FCSTD DOCUMENT  (FreeCAD 0.18R16131 (Git))
Label: temp part
License: All rights reserved
LicenseURL: http://en.wikipedia.org/wiki/All_rights_reserved
objects: Part::Part2DObjectPython×54, Part::Mirroring×27, App::DocumentObjectGroup×2
note: 81 computed .brp shape members not serialized (recipe doc carries the construction recipe); baked Part::Feature solids carry a one-line shape summary decoded from their .brp

FEATURE [Part::Part2DObjectPython] Circle  label="Hole-mount-1"  # Draft 2D object (typed FeaturePython)
  FirstAngle = 0
  LastAngle = 0
  MakeFace = false
  Placement = pos=(10,150.125,0) rot=(0,0,1;0rad)
  Radius = 1.6
FEATURE [Part::Part2DObjectPython] Rectangle  label="Edge"  # Draft 2D object (typed FeaturePython)
  ChamferSize = 0
  Columns = 1
  FilletRadius = 0
  Height = 160.12
  Length = 90
  MakeFace = false
  Rows = 1
FEATURE [Part::Part2DObjectPython] Circle001  label="Hole-mount-2"  # Draft 2D object (typed FeaturePython)
  FirstAngle = 0
  LastAngle = 0
  MakeFace = false
  Placement = pos=(80,150.125,0) rot=(0,0,1;0rad)
  Radius = 1.6
FEATURE [Part::Part2DObjectPython] Circle002  label="Hole-mount-3"  # Draft 2D object (typed FeaturePython)
  FirstAngle = 0
  LastAngle = 0
  MakeFace = false
  Placement = pos=(80,10,0) rot=(0,0,1;0rad)
  Radius = 1.6
FEATURE [Part::Part2DObjectPython] Circle003  label="Hole-mount-4"  # Draft 2D object (typed FeaturePython)
  FirstAngle = 0
  LastAngle = 0
  MakeFace = false
  Placement = pos=(10,10,0) rot=(0,0,1;0rad)
  Radius = 1.6
FEATURE [Part::Part2DObjectPython] Circle004  label="Hole-mount-VREG-board-1"  # Draft 2D object (typed FeaturePython)
  FirstAngle = 0
  LastAngle = 0
  MakeFace = false
  Placement = pos=(80,141.825,0) rot=(0,0,1;0rad)
  Radius = 1.6
FEATURE [Part::Part2DObjectPython] Circle005  label="Hole-mount-VREG-board-2"  # Draft 2D object (typed FeaturePython)
  FirstAngle = 0
  LastAngle = 0
  MakeFace = false
  Placement = pos=(10,81.825,0) rot=(0,0,1;0rad)
  Radius = 1.6
FEATURE [Part::Part2DObjectPython] Circle006  label="OLED-origin-Ja"  # Draft 2D object (typed FeaturePython)
  FirstAngle = 0
  LastAngle = 0
  MakeFace = false
  Placement = pos=(41.19,143.13,0) rot=(0,0,1;0rad)
  Radius = 0.5
FEATURE [Part::Part2DObjectPython] Circle007  label="VREG-origin-Ja"  # Draft 2D object (typed FeaturePython)
  FirstAngle = 0
  LastAngle = 0
  MakeFace = false
  Placement = pos=(68.5,80.64,0) rot=(0,0,1;0rad)
  Radius = 0.5
FEATURE [Part::Part2DObjectPython] Circle008  label="Hole-gizduinox-1"  # Draft 2D object (typed FeaturePython)
  FirstAngle = 0
  LastAngle = 0
  MakeFace = false
  Placement = pos=(18.9,57.08,0) rot=(0,0,1;0rad)
  Radius = 1.6
FEATURE [Part::Part2DObjectPython] Circle009  label="Hole-gizduinox-2"  # Draft 2D object (typed FeaturePython)
  FirstAngle = 0
  LastAngle = 0
  MakeFace = false
  Placement = pos=(78.2,70.58,0) rot=(0,0,1;0rad)
  Radius = 1.6
FEATURE [Part::Part2DObjectPython] Circle010  label="Hole-gizduinox-3"  # Draft 2D object (typed FeaturePython)
  FirstAngle = 0
  LastAngle = 0
  MakeFace = false
  Placement = pos=(78.25,24.58,0) rot=(0,0,1;0rad)
  Radius = 1.6
FEATURE [Part::Part2DObjectPython] Circle011  label="Hole-gizduinox-4"  # Draft 2D object (typed FeaturePython)
  FirstAngle = 0
  LastAngle = 0
  MakeFace = false
  Placement = pos=(18.9,29.18,0) rot=(0,0,1;0rad)
  Radius = 1.6
FEATURE [Part::Part2DObjectPython] Circle012  label="gizduino-origin-J1a"  # Draft 2D object (typed FeaturePython)
  FirstAngle = 0
  LastAngle = 0
  MakeFace = false
  Placement = pos=(21.5,72.38,0) rot=(0,0,1;0rad)
  Radius = 0.5
FEATURE [Part::Part2DObjectPython] Circle013  label="gizduino-origin-J2a"  # Draft 2D object (typed FeaturePython)
  FirstAngle = 0
  LastAngle = 0
  MakeFace = false
  Placement = pos=(43.34,72.38,0) rot=(0,0,1;0rad)
  Radius = 0.5
FEATURE [Part::Part2DObjectPython] Circle014  label="gizduino-origin-J3a"  # Draft 2D object (typed FeaturePython)
  FirstAngle = 0
  LastAngle = 0
  MakeFace = false
  Placement = pos=(39.28,24.12,0) rot=(0,0,1;0rad)
  Radius = 0.5
FEATURE [Part::Part2DObjectPython] Circle015  label="gizduino-origin-J4a"  # Draft 2D object (typed FeaturePython)
  FirstAngle = 0
  LastAngle = 0
  MakeFace = false
  Placement = pos=(16.42,24.12,0) rot=(0,0,1;0rad)
  Radius = 0.5
FEATURE [Part::Part2DObjectPython] Circle016  label="gizduino-origin-J5a"  # Draft 2D object (typed FeaturePython)
  FirstAngle = 0
  LastAngle = 0
  MakeFace = false
  Placement = pos=(11.34,67.3,0) rot=(0,0,1;0rad)
  Radius = 0.5
FEATURE [Part::Part2DObjectPython] Circle017  label="RFID-origin-J1a"  # Draft 2D object (typed FeaturePython)
  FirstAngle = 0
  LastAngle = 0
  MakeFace = false
  Placement = pos=(36.11,16.37,0) rot=(0,0,1;0rad)
  Radius = 0.5
FEATURE [Part::Part2DObjectPython] Circle018  label="RFID-origin-J1b"  # Draft 2D object (typed FeaturePython)
  FirstAngle = 0
  LastAngle = 0
  MakeFace = false
  Placement = pos=(53.89,16.37,0) rot=(0,0,1;0rad)
  Radius = 0.5
FEATURE [Part::Part2DObjectPython] Circle019  label="OLED-origin-Jb"  # Draft 2D object (typed FeaturePython)
  FirstAngle = 0
  LastAngle = 0
  MakeFace = false
  Placement = pos=(48.81,143.13,0) rot=(0,0,1;0rad)
  Radius = 0.5
FEATURE [Part::Part2DObjectPython] Circle020  label="VREG-origin-Jb"  # Draft 2D object (typed FeaturePython)
  FirstAngle = 0
  LastAngle = 0
  MakeFace = false
  Placement = pos=(73.58,80.64,0) rot=(0,0,1;0rad)
  Radius = 0.5
FEATURE [Part::Part2DObjectPython] Circle021  label="gizduino-origin-J1b"  # Draft 2D object (typed FeaturePython)
  FirstAngle = 0
  LastAngle = 0
  MakeFace = false
  Placement = pos=(39.28,72.38,0) rot=(0,0,1;0rad)
  Radius = 0.5
FEATURE [Part::Part2DObjectPython] Circle022  label="gizduino-origin-J2b"  # Draft 2D object (typed FeaturePython)
  FirstAngle = 0
  LastAngle = 0
  MakeFace = false
  Placement = pos=(61.12,72.38,0) rot=(0,0,1;0rad)
  Radius = 0.5
FEATURE [Part::Part2DObjectPython] Circle023  label="gizduino-origin-J3b"  # Draft 2D object (typed FeaturePython)
  FirstAngle = 0
  LastAngle = 0
  MakeFace = false
  Placement = pos=(51.98,24.12,0) rot=(0,0,1;0rad)
  Radius = 0.5
FEATURE [Part::Part2DObjectPython] Circle024  label="gizduino-origin-J4b"  # Draft 2D object (typed FeaturePython)
  FirstAngle = 0
  LastAngle = 0
  MakeFace = false
  Placement = pos=(34.2,24.12,0) rot=(0,0,1;0rad)
  Radius = 0.5
FEATURE [Part::Part2DObjectPython] Circle025  label="gizduino-origin-J5b"  # Draft 2D object (typed FeaturePython)
  FirstAngle = 0
  LastAngle = 0
  MakeFace = false
  Placement = pos=(8.8,67.3,0) rot=(0,0,1;0rad)
  Radius = 0.5
FEATURE [App::DocumentObjectGroup] Group
  Group = -> [Circle,Rectangle,Circle001,Circle002,Circle003,Circle004,Circle005,Circle006,Circle007,Circle008,Circle009,Circle010,Circle011,Circle012,Circle013,Circle014,Circle015,Circle016,Circle017,Circle018,Circle019,Circle020,Circle021,Circle022,Circle023,Circle024,Circle025]
FEATURE [Part::Part2DObjectPython] Circle026  label="Hole-mount-005"  # Draft 2D object (typed FeaturePython)
  FirstAngle = 0
  LastAngle = 0
  MakeFace = false
  Placement = pos=(80,10,0) rot=(0,0,1;0rad)
  Radius = 1.6
FEATURE [Part::Part2DObjectPython] Circle027  label="gizduino-origin-J2a001"  # Draft 2D object (typed FeaturePython)
  FirstAngle = 0
  LastAngle = 0
  MakeFace = false
  Placement = pos=(43.34,72.38,0) rot=(0,0,1;0rad)
  Radius = 0.5
FEATURE [Part::Part2DObjectPython] Circle028  label="Hole-mount-006"  # Draft 2D object (typed FeaturePython)
  FirstAngle = 0
  LastAngle = 0
  MakeFace = false
  Placement = pos=(80,150.125,0) rot=(0,0,1;0rad)
  Radius = 1.6
FEATURE [Part::Part2DObjectPython] Circle029  label="Hole-mount-007"  # Draft 2D object (typed FeaturePython)
  FirstAngle = 0
  LastAngle = 0
  MakeFace = false
  Placement = pos=(10,150.125,0) rot=(0,0,1;0rad)
  Radius = 1.6
FEATURE [Part::Part2DObjectPython] Circle030  label="Hole-mount-008"  # Draft 2D object (typed FeaturePython)
  FirstAngle = 0
  LastAngle = 0
  MakeFace = false
  Placement = pos=(10,10,0) rot=(0,0,1;0rad)
  Radius = 1.6
FEATURE [Part::Part2DObjectPython] Circle031  label="Hole-mount-VREG-board-003"  # Draft 2D object (typed FeaturePython)
  FirstAngle = 0
  LastAngle = 0
  MakeFace = false
  Placement = pos=(10,81.825,0) rot=(0,0,1;0rad)
  Radius = 1.6
FEATURE [Part::Part2DObjectPython] Circle032  label="VREG-origin-Ja001"  # Draft 2D object (typed FeaturePython)
  FirstAngle = 0
  LastAngle = 0
  MakeFace = false
  Placement = pos=(68.5,80.64,0) rot=(0,0,1;0rad)
  Radius = 0.5
FEATURE [Part::Part2DObjectPython] Circle033  label="gizduino-origin-J1a001"  # Draft 2D object (typed FeaturePython)
  FirstAngle = 0
  LastAngle = 0
  MakeFace = false
  Placement = pos=(21.5,72.38,0) rot=(0,0,1;0rad)
  Radius = 0.5
FEATURE [Part::Part2DObjectPython] Circle034  label="Hole-gizduinox-005"  # Draft 2D object (typed FeaturePython)
  FirstAngle = 0
  LastAngle = 0
  MakeFace = false
  Placement = pos=(78.2,70.58,0) rot=(0,0,1;0rad)
  Radius = 1.6
FEATURE [Part::Part2DObjectPython] Circle035  label="RFID-origin-J1a001"  # Draft 2D object (typed FeaturePython)
  FirstAngle = 0
  LastAngle = 0
  MakeFace = false
  Placement = pos=(36.11,16.37,0) rot=(0,0,1;0rad)
  Radius = 0.5
FEATURE [Part::Part2DObjectPython] Circle036  label="RFID-origin-J1b001"  # Draft 2D object (typed FeaturePython)
  FirstAngle = 0
  LastAngle = 0
  MakeFace = false
  Placement = pos=(53.89,16.37,0) rot=(0,0,1;0rad)
  Radius = 0.5
FEATURE [Part::Part2DObjectPython] Circle037  label="Hole-mount-VREG-board-004"  # Draft 2D object (typed FeaturePython)
  FirstAngle = 0
  LastAngle = 0
  MakeFace = false
  Placement = pos=(80,141.825,0) rot=(0,0,1;0rad)
  Radius = 1.6
FEATURE [Part::Part2DObjectPython] Circle038  label="Hole-gizduinox-006"  # Draft 2D object (typed FeaturePython)
  FirstAngle = 0
  LastAngle = 0
  MakeFace = false
  Placement = pos=(18.9,57.08,0) rot=(0,0,1;0rad)
  Radius = 1.6
FEATURE [Part::Part2DObjectPython] Circle039  label="Hole-gizduinox-007"  # Draft 2D object (typed FeaturePython)
  FirstAngle = 0
  LastAngle = 0
  MakeFace = false
  Placement = pos=(78.25,24.58,0) rot=(0,0,1;0rad)
  Radius = 1.6
FEATURE [Part::Part2DObjectPython] Circle040  label="OLED-origin-Ja001"  # Draft 2D object (typed FeaturePython)
  FirstAngle = 0
  LastAngle = 0
  MakeFace = false
  Placement = pos=(41.19,143.13,0) rot=(0,0,1;0rad)
  Radius = 0.5
FEATURE [Part::Part2DObjectPython] Circle041  label="Hole-gizduinox-008"  # Draft 2D object (typed FeaturePython)
  FirstAngle = 0
  LastAngle = 0
  MakeFace = false
  Placement = pos=(18.9,29.18,0) rot=(0,0,1;0rad)
  Radius = 1.6
FEATURE [Part::Part2DObjectPython] Rectangle001  label="Edge001"  # Draft 2D object (typed FeaturePython)
  ChamferSize = 0
  Columns = 1
  FilletRadius = 0
  Height = 160.12
  Length = 90
  MakeFace = false
  Rows = 1
FEATURE [Part::Part2DObjectPython] Circle042  label="gizduino-origin-J3a001"  # Draft 2D object (typed FeaturePython)
  FirstAngle = 0
  LastAngle = 0
  MakeFace = false
  Placement = pos=(39.28,24.12,0) rot=(0,0,1;0rad)
  Radius = 0.5
FEATURE [Part::Part2DObjectPython] Circle043  label="gizduino-origin-J5a001"  # Draft 2D object (typed FeaturePython)
  FirstAngle = 0
  LastAngle = 0
  MakeFace = false
  Placement = pos=(11.34,67.3,0) rot=(0,0,1;0rad)
  Radius = 0.5
FEATURE [Part::Part2DObjectPython] Circle044  label="OLED-origin-Jb001"  # Draft 2D object (typed FeaturePython)
  FirstAngle = 0
  LastAngle = 0
  MakeFace = false
  Placement = pos=(48.81,143.13,0) rot=(0,0,1;0rad)
  Radius = 0.5
FEATURE [Part::Part2DObjectPython] Circle045  label="gizduino-origin-J4a001"  # Draft 2D object (typed FeaturePython)
  FirstAngle = 0
  LastAngle = 0
  MakeFace = false
  Placement = pos=(16.42,24.12,0) rot=(0,0,1;0rad)
  Radius = 0.5
FEATURE [Part::Part2DObjectPython] Circle046  label="gizduino-origin-J1b001"  # Draft 2D object (typed FeaturePython)
  FirstAngle = 0
  LastAngle = 0
  MakeFace = false
  Placement = pos=(39.28,72.38,0) rot=(0,0,1;0rad)
  Radius = 0.5
FEATURE [Part::Part2DObjectPython] Circle047  label="VREG-origin-Jb001"  # Draft 2D object (typed FeaturePython)
  FirstAngle = 0
  LastAngle = 0
  MakeFace = false
  Placement = pos=(73.58,80.64,0) rot=(0,0,1;0rad)
  Radius = 0.5
FEATURE [Part::Part2DObjectPython] Circle048  label="gizduino-origin-J2b001"  # Draft 2D object (typed FeaturePython)
  FirstAngle = 0
  LastAngle = 0
  MakeFace = false
  Placement = pos=(61.12,72.38,0) rot=(0,0,1;0rad)
  Radius = 0.5
FEATURE [Part::Part2DObjectPython] Circle049  label="gizduino-origin-J3b001"  # Draft 2D object (typed FeaturePython)
  FirstAngle = 0
  LastAngle = 0
  MakeFace = false
  Placement = pos=(51.98,24.12,0) rot=(0,0,1;0rad)
  Radius = 0.5
FEATURE [Part::Part2DObjectPython] Circle050  label="gizduino-origin-J5b001"  # Draft 2D object (typed FeaturePython)
  FirstAngle = 0
  LastAngle = 0
  MakeFace = false
  Placement = pos=(8.8,67.3,0) rot=(0,0,1;0rad)
  Radius = 0.5
FEATURE [Part::Part2DObjectPython] Circle051  label="gizduino-origin-J4b001"  # Draft 2D object (typed FeaturePython)
  FirstAngle = 0
  LastAngle = 0
  MakeFace = false
  Placement = pos=(34.2,24.12,0) rot=(0,0,1;0rad)
  Radius = 0.5
FEATURE [App::DocumentObjectGroup] Group001  label="Mirror"
  Group = -> [Circle029,Rectangle001,Circle028,Circle026,Circle030,Circle037,Circle031,Circle040,Circle032,Circle038,Circle034,Circle039,Circle041,Circle033,Circle027,Circle042,Circle045,Circle043,Circle035,Circle036,Circle044,Circle047,Circle046,Circle048,Circle049,Circle051,Circle050]
FEATURE [Part::Mirroring] mirror  label="Mirror of Hole-mount-007"
  Base = (90,160.12,0)
  Normal = (-1,1e-16,0)
  Source = -> Circle029
FEATURE [Part::Mirroring] mirror001  label="Mirror of Hole-mount-005"
  Base = (90,160.12,0)
  Normal = (-1,1e-16,0)
  Source = -> Circle026
FEATURE [Part::Mirroring] mirror002  label="Mirror of gizduino-origin-J4a001"
  Base = (90,160.12,0)
  Normal = (-1,1e-16,0)
  Source = -> Circle045
FEATURE [Part::Mirroring] mirror003  label="Mirror of Edge001"
  Base = (90,160.12,0)
  Normal = (-1,1e-16,0)
  Source = -> Rectangle001
FEATURE [Part::Mirroring] mirror004  label="Mirror of VREG-origin-Jb001"
  Base = (90,160.12,0)
  Normal = (-1,1e-16,0)
  Source = -> Circle047
FEATURE [Part::Mirroring] mirror005  label="Mirror of OLED-origin-Ja001"
  Base = (90,160.12,0)
  Normal = (-1,1e-16,0)
  Source = -> Circle040
FEATURE [Part::Mirroring] mirror006  label="Mirror of Hole-gizduinox-006"
  Base = (90,160.12,0)
  Normal = (-1,1e-16,0)
  Source = -> Circle038
FEATURE [Part::Mirroring] mirror007  label="Mirror of Hole-gizduinox-007"
  Base = (90,160.12,0)
  Normal = (-1,1e-16,0)
  Source = -> Circle039
FEATURE [Part::Mirroring] mirror008  label="Mirror of gizduino-origin-J5a001"
  Base = (90,160.12,0)
  Normal = (-1,1e-16,0)
  Source = -> Circle043
FEATURE [Part::Mirroring] mirror009  label="Mirror of Hole-gizduinox-008"
  Base = (90,160.12,0)
  Normal = (-1,1e-16,0)
  Source = -> Circle041
FEATURE [Part::Mirroring] mirror010  label="Mirror of gizduino-origin-J1b001"
  Base = (90,160.12,0)
  Normal = (-1,1e-16,0)
  Source = -> Circle046
FEATURE [Part::Mirroring] mirror011  label="Mirror of Hole-mount-006"
  Base = (90,160.12,0)
  Normal = (-1,1e-16,0)
  Source = -> Circle028
FEATURE [Part::Mirroring] mirror012  label="Mirror of gizduino-origin-J5b001"
  Base = (90,160.12,0)
  Normal = (-1,1e-16,0)
  Source = -> Circle050
FEATURE [Part::Mirroring] mirror013  label="Mirror of Hole-mount-008"
  Base = (90,160.12,0)
  Normal = (-1,1e-16,0)
  Source = -> Circle030
FEATURE [Part::Mirroring] mirror014  label="Mirror of Hole-mount-VREG-board-003"
  Base = (90,160.12,0)
  Normal = (-1,1e-16,0)
  Source = -> Circle031
FEATURE [Part::Mirroring] mirror015  label="Mirror of VREG-origin-Ja001"
  Base = (90,160.12,0)
  Normal = (-1,1e-16,0)
  Source = -> Circle032
FEATURE [Part::Mirroring] mirror016  label="Mirror of Hole-gizduinox-005"
  Base = (90,160.12,0)
  Normal = (-1,1e-16,0)
  Source = -> Circle034
FEATURE [Part::Mirroring] mirror017  label="Mirror of OLED-origin-Jb001"
  Base = (90,160.12,0)
  Normal = (-1,1e-16,0)
  Source = -> Circle044
FEATURE [Part::Mirroring] mirror018  label="Mirror of gizduino-origin-J2a001"
  Base = (90,160.12,0)
  Normal = (-1,1e-16,0)
  Source = -> Circle027
FEATURE [Part::Mirroring] mirror019  label="Mirror of gizduino-origin-J1a001"
  Base = (90,160.12,0)
  Normal = (-1,1e-16,0)
  Source = -> Circle033
FEATURE [Part::Mirroring] mirror020  label="Mirror of RFID-origin-J1a001"
  Base = (90,160.12,0)
  Normal = (-1,1e-16,0)
  Source = -> Circle035
FEATURE [Part::Mirroring] mirror021  label="Mirror of RFID-origin-J1b001"
  Base = (90,160.12,0)
  Normal = (-1,1e-16,0)
  Source = -> Circle036
FEATURE [Part::Mirroring] mirror022  label="Mirror of Hole-mount-VREG-board-004"
  Base = (90,160.12,0)
  Normal = (-1,1e-16,0)
  Source = -> Circle037
FEATURE [Part::Mirroring] mirror023  label="Mirror of gizduino-origin-J3a001"
  Base = (90,160.12,0)
  Normal = (-1,1e-16,0)
  Source = -> Circle042
FEATURE [Part::Mirroring] mirror024  label="Mirror of gizduino-origin-J2b001"
  Base = (90,160.12,0)
  Normal = (-1,1e-16,0)
  Source = -> Circle048
FEATURE [Part::Mirroring] mirror025  label="Mirror of gizduino-origin-J3b001"
  Base = (90,160.12,0)
  Normal = (-1,1e-16,0)
  Source = -> Circle049
FEATURE [Part::Mirroring] mirror026  label="Mirror of gizduino-origin-J4b001"
  Base = (90,160.12,0)
  Normal = (-1,1e-16,0)
  Source = -> Circle051
